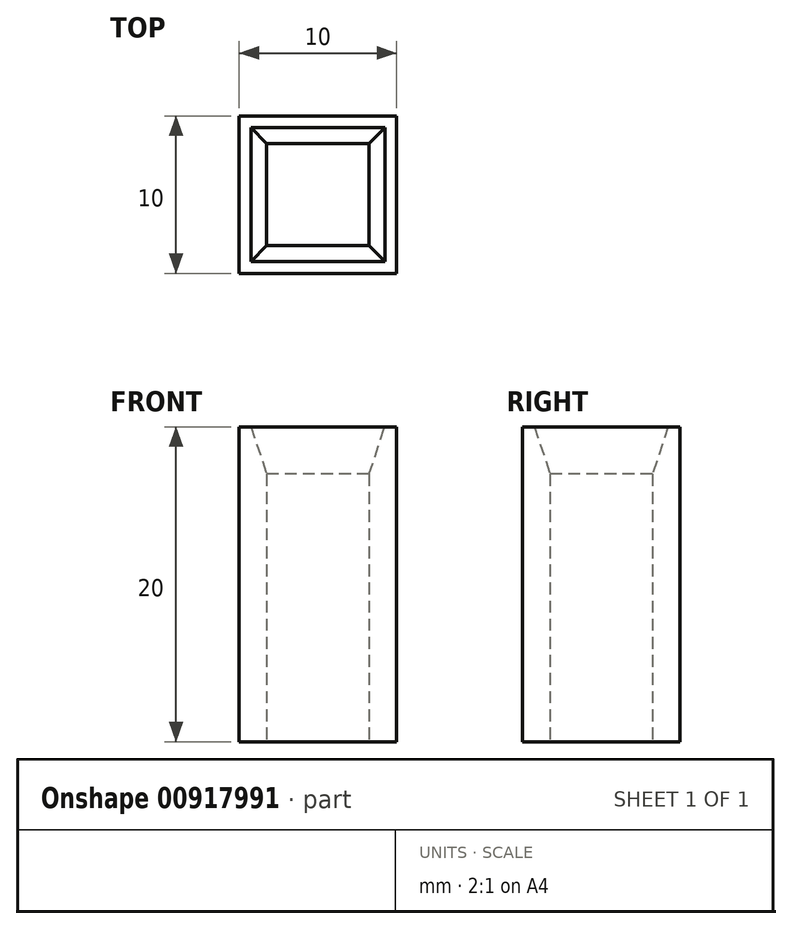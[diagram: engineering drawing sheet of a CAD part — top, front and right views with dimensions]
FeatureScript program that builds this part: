
annotation { "Feature Type Name" : "Feature", "Feature Type Description" : "" }
export const myFeature = defineFeature(function(context is Context, id is Id, definition is map)
    precondition{}
    {
        {
            var Q0;
            Q0=qCreatedBy(makeId("Top.planeOp"),FACE);
            var sketch = newSketch(context, id + "F0", { "sketchPlane" : qUnion([Q0])});
            skLineSegment(sketch, "E0.bottom", {"start": v(-5, 5) * mm, "end": v(5, 5) * mm});
            skLineSegment(sketch, "E0.top", {"start": v(-5, -5) * mm, "end": v(5, -5) * mm});
            skLineSegment(sketch, "E0.left", {"start": v(-5, 5) * mm, "end": v(-5, -5) * mm});
            skLineSegment(sketch, "E0.right", {"start": v(5, 5) * mm, "end": v(5, -5) * mm});
            skPoint(sketch, "E0.middle", {"position": v(0, 0) * mm});
            skLineSegment(sketch, "E1.bottom", {"start": v(-3.25, 3.25) * mm, "end": v(3.25, 3.25) * mm});
            skLineSegment(sketch, "E1.top", {"start": v(-3.25, -3.25) * mm, "end": v(3.25, -3.25) * mm});
            skLineSegment(sketch, "E1.left", {"start": v(-3.25, 3.25) * mm, "end": v(-3.25, -3.25) * mm});
            skLineSegment(sketch, "E1.right", {"start": v(3.25, 3.25) * mm, "end": v(3.25, -3.25) * mm});
            skLineSegment(sketch, "E2.bottom", {"start": v(-3.75, 3.75) * mm, "end": v(3.75, 3.75) * mm});
            skLineSegment(sketch, "E2.top", {"start": v(-3.75, -3.75) * mm, "end": v(3.75, -3.75) * mm});
            skLineSegment(sketch, "E2.left", {"start": v(-3.75, 3.75) * mm, "end": v(-3.75, -3.75) * mm});
            skLineSegment(sketch, "E2.right", {"start": v(3.75, 3.75) * mm, "end": v(3.75, -3.75) * mm});
            skSolve(sketch);
        }
        {
            var Q0;
            Q0 = qSketchRegion(id + "F0", true);
            var Q1;
            Q1=makeQuery(id+"F0.imprint","IMPRINT",FACE,{"disambiguationData":[TD([[makeQuery(id+"F0.imprint","IMPRINT",EDGE,{"derivedFrom":sQuery(id+"F0.wireOp",EDGE,"E1.bottom")}),1.0]])]});
            extrude(context, id + "F1", {"entities" : qUnion([Q0, Q1]), "depth" : 20 * mm, "offsetDistance" : 25 * mm});
        }
        {
            var Q0;
            Q0=makeQuery(id+"F1.opExtrude","CAP_EDGE",EDGE,{"disambiguationData":[OSD([sQuery(id+"F0.wireOp",EDGE,"E1.left")])],"isStart":false});
            chamfer(context, id + "F2", {"entities" : qUnion([Q0]), "chamferType" : ChamferType.TWO_OFFSETS, "width1" : 3 * mm, "oppositeDirection" : false, "width2" : 1 * mm, "tangentPropagation" : true});
        }
        {
            var Q0;
            Q0=makeQuery(id+"F1.opExtrude","CAP_EDGE",EDGE,{"disambiguationData":[OSD([sQuery(id+"F0.wireOp",EDGE,"E1.bottom")])],"isStart":false});
            chamfer(context, id + "F3", {"entities" : qUnion([Q0]), "chamferType" : ChamferType.TWO_OFFSETS, "width1" : 3 * mm, "oppositeDirection" : true, "width2" : 1 * mm, "tangentPropagation" : true});
        }
        {
            var Q0;
            Q0=makeQuery(id+"F1.opExtrude","CAP_EDGE",EDGE,{"disambiguationData":[OSD([sQuery(id+"F0.wireOp",EDGE,"E1.right")])],"isStart":false});
            chamfer(context, id + "F4", {"entities" : qUnion([Q0]), "chamferType" : ChamferType.TWO_OFFSETS, "width1" : 3 * mm, "oppositeDirection" : true, "width2" : 1 * mm, "tangentPropagation" : true});
        }
        {
            var Q0;
            Q0=makeQuery(id+"F1.opExtrude","CAP_EDGE",EDGE,{"disambiguationData":[OSD([sQuery(id+"F0.wireOp",EDGE,"E1.top")])],"isStart":false});
            chamfer(context, id + "F5", {"entities" : qUnion([Q0]), "chamferType" : ChamferType.TWO_OFFSETS, "width1" : 3 * mm, "oppositeDirection" : false, "width2" : 1 * mm, "tangentPropagation" : true});
        }
    });
